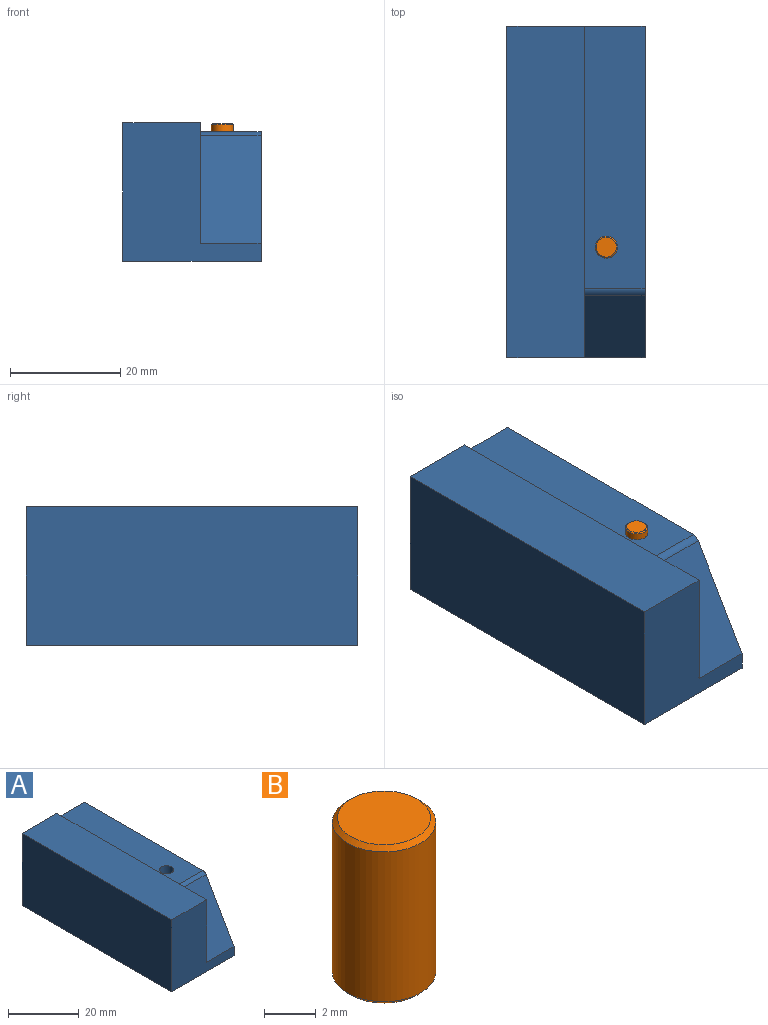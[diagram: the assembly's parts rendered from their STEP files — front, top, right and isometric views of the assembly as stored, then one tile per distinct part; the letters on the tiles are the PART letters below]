
ASSEMBLY  parts=2 mates=1
PART A: 12 faces, bbox 25x60x25 mm
  f0: plane 25x25mm, normal (0,-1,0), area 385.7mm2, adj f1,f3,f5,f6,f7,f10
  f1: plane 60x23.4mm, normal (1,0,0), area 1286.7mm2, adj f0,f2,f4,f5,f10,f11
  f2: plane 47.5x11mm, normal (0,0,1), area 509.9mm2, adj f1,f4,f7,f8,f11
  f3: plane 60x14mm, normal (0,0,1), area 840mm2, adj f0,f4,f6,f7
  f4: plane 25x25mm, normal (0,1,0), area 607.4mm2, adj f1,f2,f3,f5,f6,f7
  f5: plane 60x25mm, normal (0,0,-1), area 1500mm2, adj f0,f1,f4,f6
  f6: plane 60x25mm, normal (-1,0,0), area 1500mm2, adj f0,f3,f4,f5
  f7: plane 60x21.75mm, normal (1,0,0), area 213.3mm2, adj f0,f2,f3,f4,f10,f11
  f8: cylinder r=2mm len=6mm, axis (0,0,1), area 75.4mm2, adj f2,f9
  f9: plane 4x4mm, normal (0,0,1), area 12.6mm2, adj f8
  f10: plane 19.4x11.2mm, normal (0,-0.87,0.5), area 246.4mm2, adj f0,f1,f7,f11
  f11: cylinder r=1.5mm len=11mm, axis (1,0,0), area 17.3mm2, adj f1,f2,f7,f10
PART B: 5 faces, bbox 4x4x7.5 mm
  f0: cylinder r=2mm len=7.1mm, axis (0,0,-1), area 89.2mm2, adj f3,f4
  f1: plane 3.6x3.6mm, normal (0,0,1), area 10.2mm2, adj f4
  f2: plane 3.6x3.6mm, normal (0,0,-1), area 10.2mm2, adj f3
  f3: cone r=2mm half-angle=45deg, axis (0,0,1), area 3.4mm2, adj f0,f2
  f4: cone r=1.8mm half-angle=45deg, axis (0,0,-1), area 3.4mm2, adj f0,f1
PLACE A t=(0.38,2.65,-0.1)mm fixed
PLACE B t=(-6.62,22.65,-7.7)mm
MATE fastened A.f8 <-> B.f0  axis (0,0,1) through (-6.62,22.65,-7.7)mm
